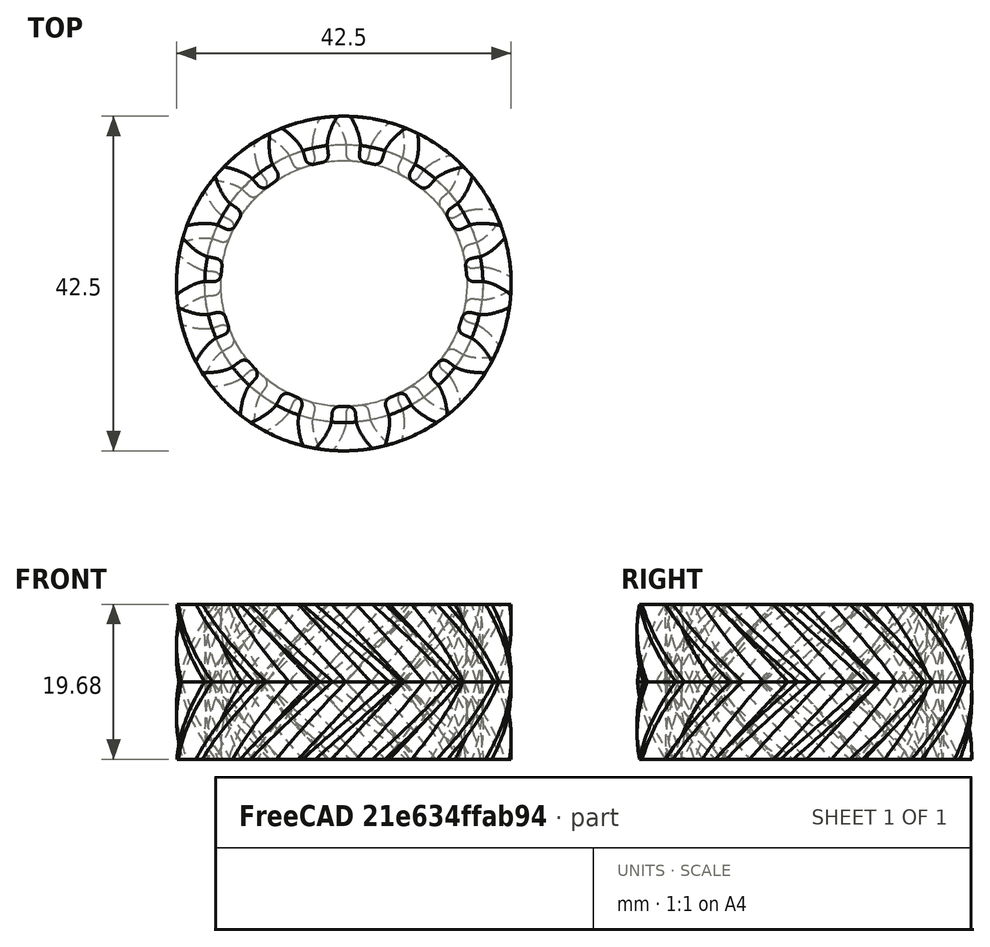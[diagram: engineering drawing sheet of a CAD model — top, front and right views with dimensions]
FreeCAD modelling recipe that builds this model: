
FCSTD DOCUMENT  (FreeCAD 0.20R29177 +426 (Git))
Label: Tren Engranaje Chevron
License: All rights reserved
LicenseURL: http://en.wikipedia.org/wiki/All_rights_reserved
objects: Part::Part2DObjectPython×7, Part::Mirroring×2, Part::Loft×1, Part::MultiFuse×1
note: 11 computed .brp shape members not serialized (recipe doc carries the construction recipe); baked Part::Feature solids carry a one-line shape summary decoded from their .brp

FEATURE [Part::Part2DObjectPython] InvoluteGear  # Draft 2D object (typed FeaturePython)
  ExternalGear = true
  HighPrecision = true
  Modules = 2.5
  NumberOfTeeth = 15
  PressureAngle = 20
FEATURE [Part::Part2DObjectPython] InvoluteGear001  # Draft 2D object (typed FeaturePython)
  ExternalGear = true
  HighPrecision = true
  Modules = 2.5
  NumberOfTeeth = 15
  Placement = pos=(0,0,1.64) rot=(0,0,1;0.087266rad)
  PressureAngle = 20
FEATURE [Part::Part2DObjectPython] InvoluteGear002  # Draft 2D object (typed FeaturePython)
  ExternalGear = true
  HighPrecision = true
  Modules = 2.5
  NumberOfTeeth = 15
  Placement = pos=(0,0,3.28) rot=(0,0,1;0.174533rad)
  PressureAngle = 20
FEATURE [Part::Part2DObjectPython] InvoluteGear003  # Draft 2D object (typed FeaturePython)
  ExternalGear = true
  HighPrecision = true
  Modules = 2.5
  NumberOfTeeth = 15
  Placement = pos=(0,0,4.92) rot=(0,0,1;0.261799rad)
  PressureAngle = 20
FEATURE [Part::Part2DObjectPython] InvoluteGear004  # Draft 2D object (typed FeaturePython)
  ExternalGear = true
  HighPrecision = true
  Modules = 2.5
  NumberOfTeeth = 15
  Placement = pos=(0,0,6.56) rot=(0,0,1;0.349066rad)
  PressureAngle = 20
FEATURE [Part::Part2DObjectPython] InvoluteGear005  # Draft 2D object (typed FeaturePython)
  ExternalGear = true
  HighPrecision = true
  Modules = 2.5
  NumberOfTeeth = 15
  Placement = pos=(0,0,8.2) rot=(0,0,1;0.436332rad)
  PressureAngle = 20
FEATURE [Part::Part2DObjectPython] InvoluteGear006  # Draft 2D object (typed FeaturePython)
  ExternalGear = true
  HighPrecision = true
  Modules = 2.5
  NumberOfTeeth = 15
  Placement = pos=(0,0,9.84) rot=(0,0,1;0.523599rad)
  PressureAngle = 20
FEATURE [Part::Loft] Loft
  Closed = false
  MaxDegree = 5
  Ruled = false
  Sections = -> [InvoluteGear,InvoluteGear001,InvoluteGear002,InvoluteGear003,InvoluteGear004,InvoluteGear005,InvoluteGear006]
  Solid = true
FEATURE [Part::Mirroring] Part__Mirroring  label="Loft (Mirror #1)"
  Base = (0,0,0)
  Normal = (0,0,1)
  Source = -> Loft
FEATURE [Part::MultiFuse] Fusion
  Placement = pos=(37.5,0,0) rot=(0,0,1;0rad)
  Shapes = -> [Part__Mirroring,Loft]
FEATURE [Part::Mirroring] Part__Mirroring001  label="Fusion (Mirror #2)"
  Base = (0,0,0)
  Normal = (0,1,0)
  Placement = pos=(37.5,0,0) rot=(0,0,1;0rad)
  Source = -> Fusion
